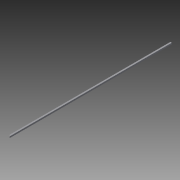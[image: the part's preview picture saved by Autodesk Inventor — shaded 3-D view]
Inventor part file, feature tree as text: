
AUTODESK INVENTOR PART (.ipt)
format: ipt  version: 2015 SP1 (Build 190203100, 203)  size: 87,040 bytes
history: native  units: mm
features: extrude x2, sketch x2
ambient origin geometry x8: Origin, YZ Plane, XZ Plane, XY Plane, X Axis, Y Axis, Z Axis, Center Point
bodies: Solid1 (feature_tree)
feature tree (4):
  extrude  "Extrusion1"  Depth=20.0mm
  extrude  "Extrusion2"  Depth=2.0mm TaperAngle=0.0deg
  sketch  "Sketch1"  dims[d0=20.0mm d1=20.0mm]
  sketch  "Sketch2"  dims[d2=2.0mm d3=2200.0mm d4=0.0mm d5=45.0deg d6=1700.0mm d7=0.0mm]
